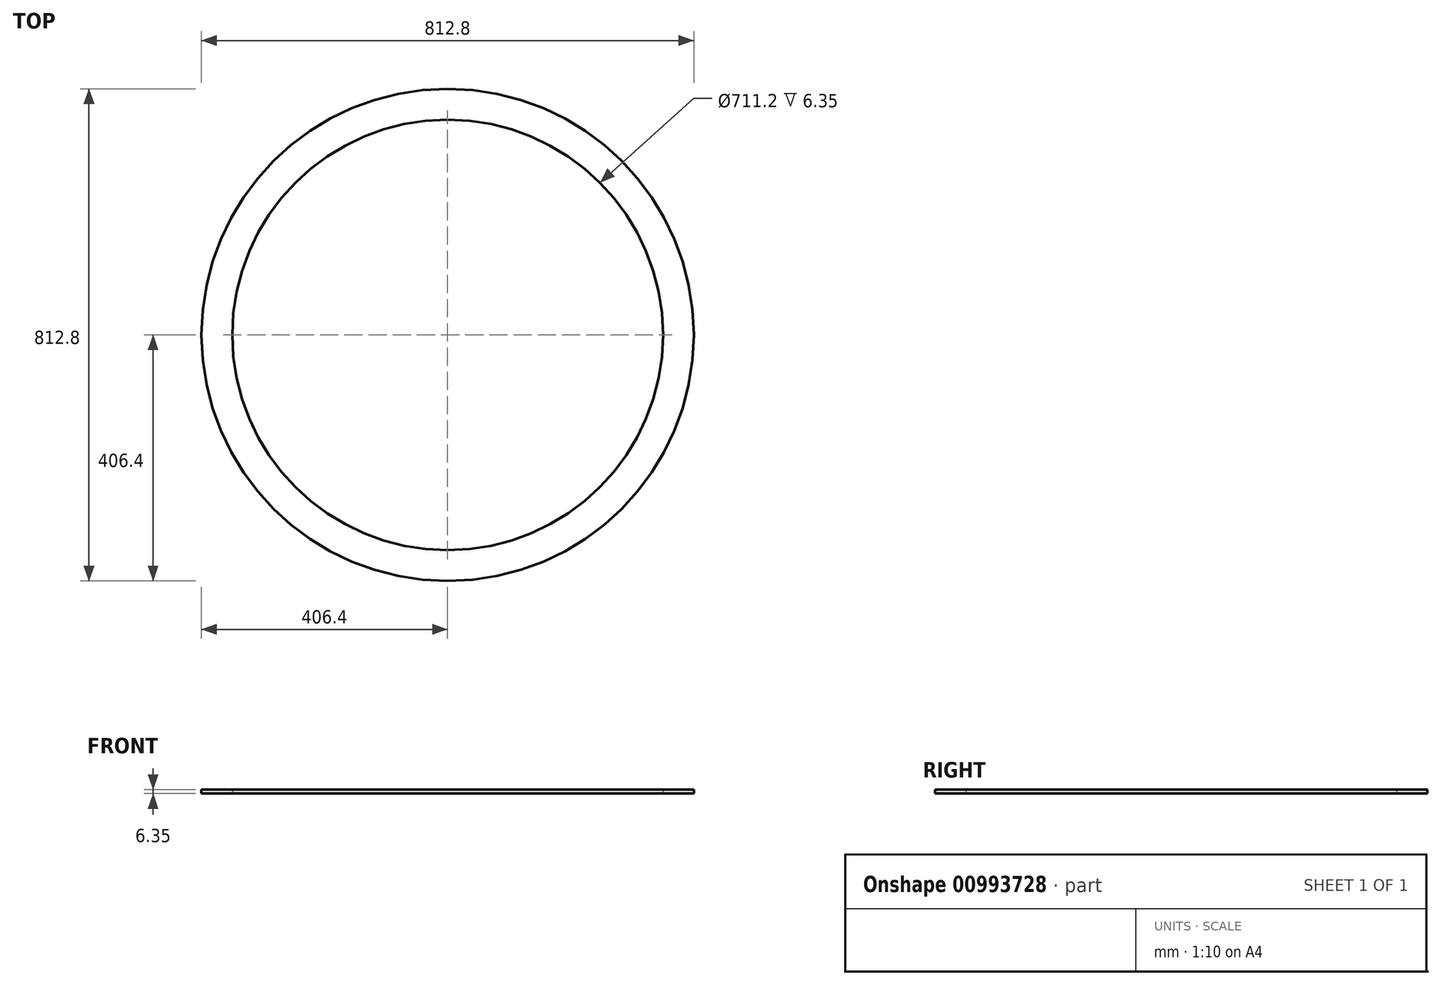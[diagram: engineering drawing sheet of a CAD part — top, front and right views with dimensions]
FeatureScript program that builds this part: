
annotation { "Feature Type Name" : "Feature", "Feature Type Description" : "" }
export const myFeature = defineFeature(function(context is Context, id is Id, definition is map)
    precondition{}
    {
        {
            var Q0;
            Q0=qCreatedBy(makeId("Top.planeOp"),FACE);
            var sketch = newSketch(context, id + "F0", { "sketchPlane" : qUnion([Q0])});
            skCircle(sketch, "E0", {"center": v(0, 0) * mm, "radius": 406.4 * mm});
            skCircle(sketch, "E1", {"center": v(0, 0) * mm, "radius": 355.6 * mm});
            skSolve(sketch);
        }
        {
            var Q0;
            Q0=makeQuery(id+"F0.imprint","IMPRINT",FACE,{"disambiguationData":[TD([[makeQuery(id+"F0.imprint","IMPRINT",EDGE,{"derivedFrom":sQuery(id+"F0.wireOp",EDGE,"E0")}),1.0]])]});
            extrude(context, id + "F1", {"entities" : qUnion([Q0]), "depth" : 6.35 * mm, "offsetDistance" : 25.4 * mm});
        }
    });
